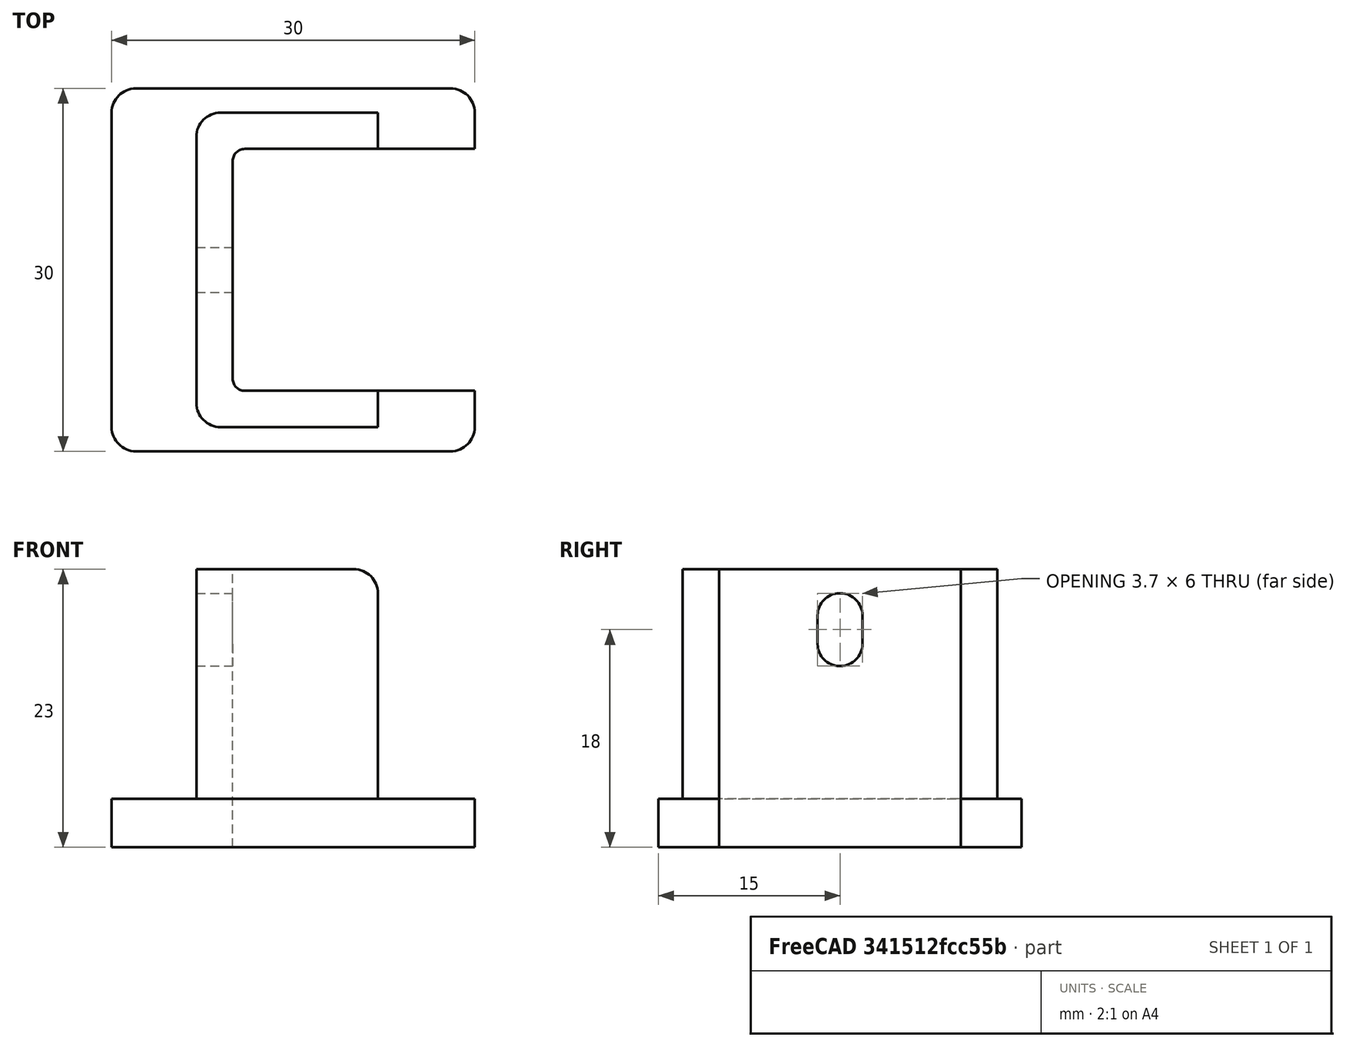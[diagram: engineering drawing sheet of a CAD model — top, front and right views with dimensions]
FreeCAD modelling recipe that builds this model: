
FCSTD DOCUMENT  (FreeCAD 0.20R29410 (Git))
Label: flood_sensor
License: All rights reserved
LicenseURL: http://en.wikipedia.org/wiki/All_rights_reserved
objects: Part::Box×4, Part::Fillet×4, Part::MultiFuse×2, Part::Cut×1
note: 11 computed .brp shape members not serialized (recipe doc carries the construction recipe); baked Part::Feature solids carry a one-line shape summary decoded from their .brp

FEATURE [Part::Box] Box  label="Cube"
  AttacherType = Attacher::AttachEngine3D
  Height = 50
  Length = 50
  Placement = pos=(0,-10,0) rot=(0,0,1;0rad)
  Width = 20
  expr: .Placement.Base.y = -Width / 2
FEATURE [Part::Fillet] Fillet
  Base = -> Box
  Edges = 2 edges r=1: [Edge1,Edge3]
FEATURE [Part::Box] Box001  label="Cube001"
  AttacherType = Attacher::AttachEngine3D
  Height = 23
  Length = 15
  Placement = pos=(-3,-13,0) rot=(0,0,1;0rad)
  Width = 26
  expr: .Placement.Base.y = -Width / 2
  expr: Width = <<Cube>>.Width + 6mm
FEATURE [Part::Fillet] Fillet001
  Base = -> Box001
  Edges = 3 edges r=2: [Edge1,Edge3,Edge6]
FEATURE [Part::Box] Box002  label="Cube002"
  AttacherType = Attacher::AttachEngine3D
  Height = 4
  Length = 30
  Placement = pos=(-10,-15,0) rot=(0,0,1;0rad)
  Width = 30
  expr: .Placement.Base.y = -Width / 2
FEATURE [Part::Fillet] Fillet002
  Base = -> Box002
  Edges = 4 edges r=2: [Edge1,Edge3,Edge5,Edge7]
FEATURE [Part::MultiFuse] Fusion
  Shapes = -> [Fillet001,Fillet002]
FEATURE [Part::Box] Box003  label="Cube003"
  AttacherType = Attacher::AttachEngine3D
  Height = 6
  Length = 50
  Placement = pos=(-20,-1.85,15) rot=(0,0,1;0rad)
  Width = 3.7
  expr: .Placement.Base.y = -Width / 2
  expr: .Placement.Base.z = 18mm - Height / 2
FEATURE [Part::Fillet] Fillet003
  Base = -> Box003
  Edges = 4 edges r=1.8: [Edge9,Edge10,Edge11,Edge12]
FEATURE [Part::MultiFuse] Fusion001
  Shapes = -> [Fillet,Fillet003]
FEATURE [Part::Cut] Cut  label="flood sensor"
  Base = -> Fusion
  Tool = -> Fusion001
